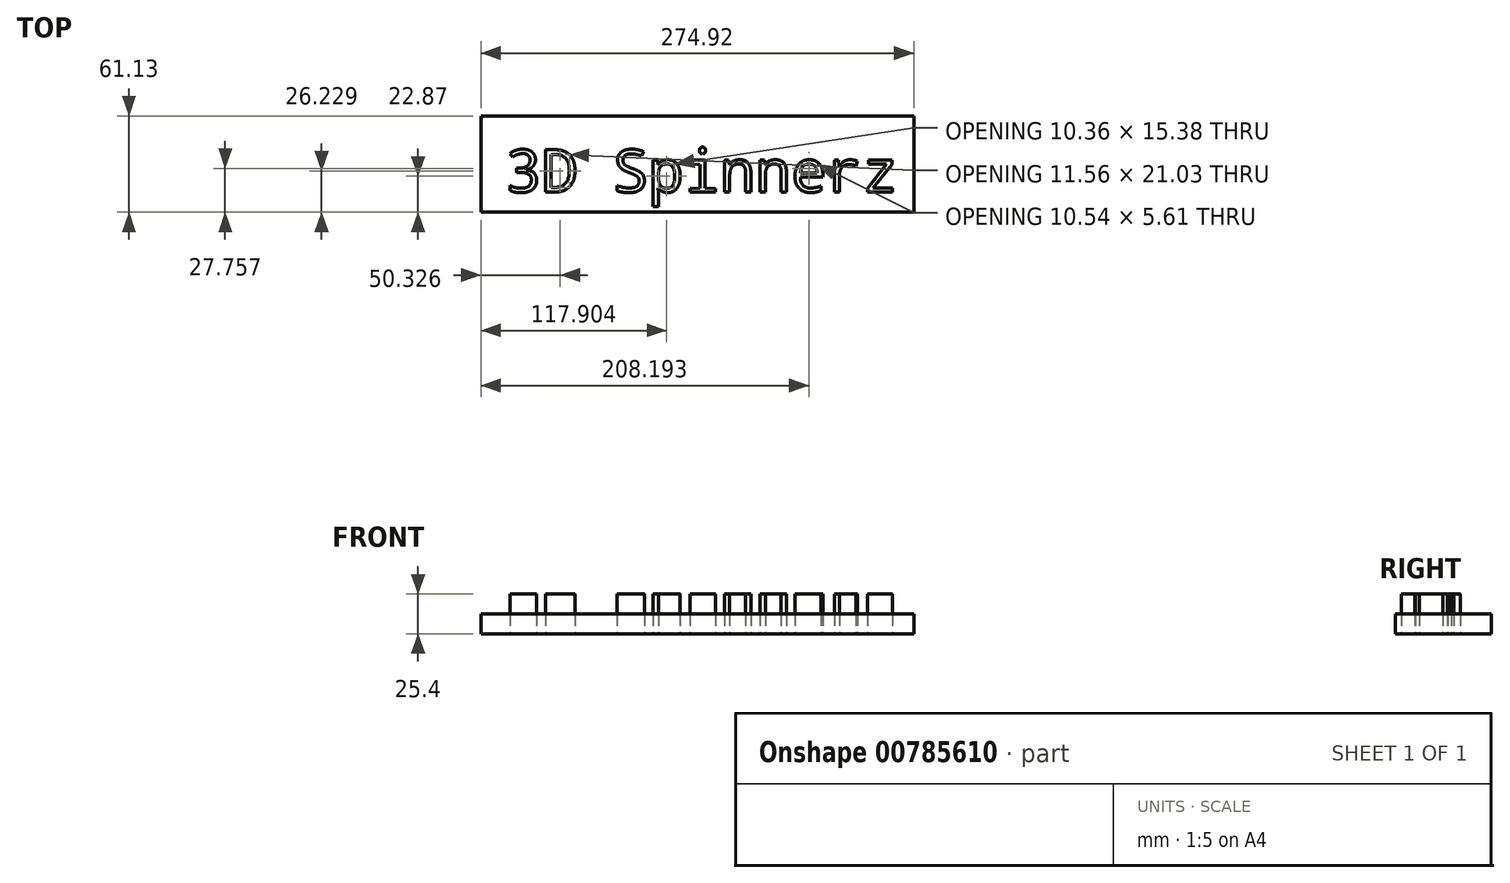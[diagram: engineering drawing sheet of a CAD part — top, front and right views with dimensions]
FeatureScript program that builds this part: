
annotation { "Feature Type Name" : "Feature", "Feature Type Description" : "" }
export const myFeature = defineFeature(function(context is Context, id is Id, definition is map)
    precondition{}
    {
        {
            var Q0;
            Q0=qCreatedBy(makeId("Top.planeOp"),FACE);
            var sketch = newSketch(context, id + "F0", { "sketchPlane" : qUnion([Q0])});
            skText(sketch, "E0", { "text": "3D Spinnerz", "fontName": "DroidSansMono.ttf"});
            const initialGuessF0  = {"E0": [-0.0638, 0.02505, 1, 0, 0.02713]};
            skSetInitialGuess(sketch, initialGuessF0);
            skSolve(sketch);
        }
        {
            var Q0;
            Q0 = qSketchRegion(id + "F0", true);
            extrude(context, id + "F1", {"entities" : qUnion([Q0]), "depth" : 25.4 * mm, "offsetDistance" : 25.4 * mm});
        }
        {
            var Q0;
            Q0=qCreatedBy(makeId("Top.planeOp"),FACE);
            var sketch = newSketch(context, id + "F2", { "sketchPlane" : qUnion([Q0])});
            skLineSegment(sketch, "E1.bottom", {"start": v(-79.8, 73.4) * mm, "end": v(195.1, 73.4) * mm});
            skLineSegment(sketch, "E1.top", {"start": v(-79.8, 12.28) * mm, "end": v(195.1, 12.28) * mm});
            skLineSegment(sketch, "E1.left", {"start": v(-79.8, 73.4) * mm, "end": v(-79.8, 12.28) * mm});
            skLineSegment(sketch, "E1.right", {"start": v(195.1, 73.4) * mm, "end": v(195.1, 12.28) * mm});
            skSolve(sketch);
        }
        {
            var Q0;
            Q0 = qSketchRegion(id + "F2", true);
            extrude(context, id + "F3", {"entities" : qUnion([Q0]), "depth" : 12.7 * mm, "offsetDistance" : 25.4 * mm});
        }
    });
